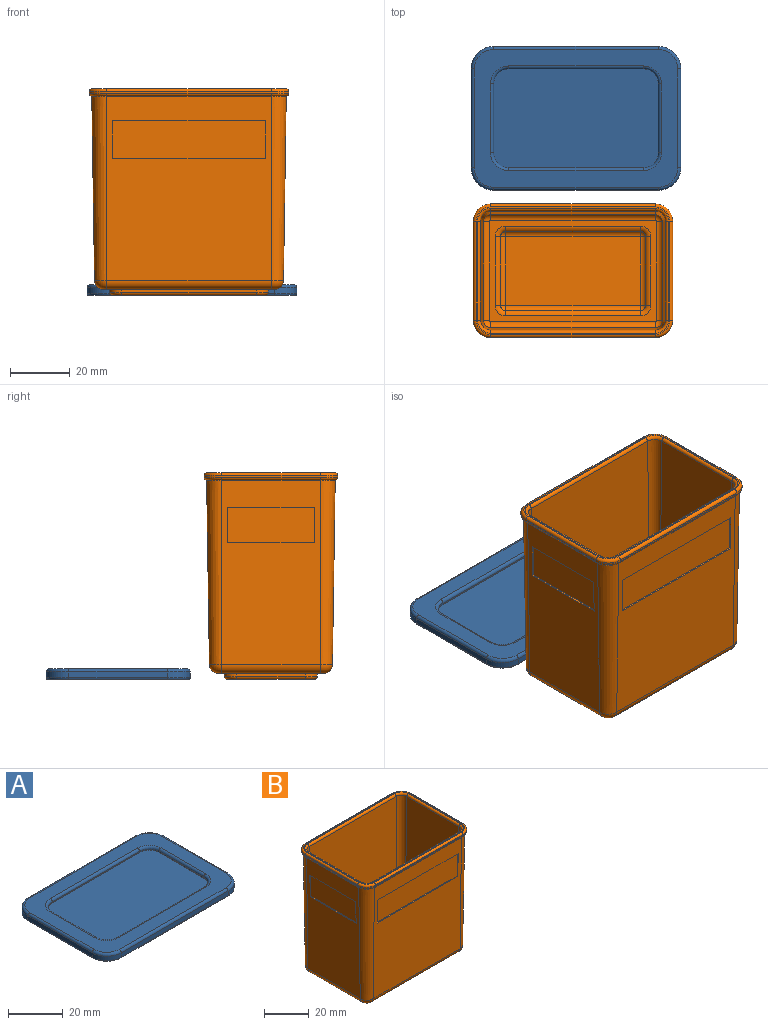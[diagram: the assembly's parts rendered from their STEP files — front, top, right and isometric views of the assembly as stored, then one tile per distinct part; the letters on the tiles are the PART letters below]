
ASSEMBLY  parts=2 mates=1
PART A: 61 faces, bbox 71.2x49.2x3.5 mm
  f0: plane 68x46mm, normal (0,0,-1), area 950.8mm2, adj f5,f6,f7,f9,f10,f11,f19,f20
  f1: plane 55x2mm, normal (0,1,0), area 110mm2, adj f2,f17,f41,f49
  f2: cylinder r=7.5mm len=7.5mm, axis (0,0,-1), area 23.6mm2, adj f1,f3,f39,f47
  f3: plane 33x2mm, normal (-1,0,0), area 66mm2, adj f2,f26,f37,f45
  f4: plane 68x46mm, normal (0,0,1), area 1127.6mm2, adj f37,f38,f39,f40,f41,f42,f43,f44
  f5: plane 55x2.5mm, normal (0,-1,0), area 137.5mm2, adj f0,f6,f8,f19
  f6: cylinder r=6.5mm len=6.5mm, axis (0,0,1), area 25.5mm2, adj f0,f5,f7,f8
  f7: plane 33x2.5mm, normal (1,0,0), area 82.5mm2, adj f0,f6,f8,f28
  f8: plane 69x47mm, normal (0,0,-1), area 109.2mm2, adj f5,f6,f7,f19,f20,f27,f28,f34
  f9: plane 45x2.5mm, normal (0,1,0), area 112.5mm2, adj f0,f11,f12,f22
  f10: plane 23x2.5mm, normal (-1,0,0), area 57.5mm2, adj f0,f11,f12,f30
  f11: cylinder r=7mm len=7mm, axis (0,0,1), area 27.5mm2, adj f0,f9,f10,f12
  f12: plane 59x37mm, normal (0,0,-1), area 2140.9mm2, adj f9,f10,f11,f21,f22,f29,f30,f35
  f13: plane 45x0.5mm, normal (0,-1,0), area 22.5mm2, adj f14,f16,f23,f53
  f14: cylinder r=5mm len=5mm, axis (0,0,1), area 3.9mm2, adj f13,f15,f16,f54
  f15: plane 23x0.5mm, normal (1,0,0), area 11.5mm2, adj f14,f16,f32,f56
  f16: plane 55x33mm, normal (0,0,1), area 1793.5mm2, adj f13,f14,f15,f23,f24,f31,f32,f36
  f17: cylinder r=7.5mm len=7.5mm, axis (0,0,-1), area 23.6mm2, adj f1,f18,f43,f51
  f18: plane 33x2mm, normal (1,0,0), area 66mm2, adj f17,f33,f44,f52
  f19: cylinder r=6.5mm len=6.5mm, axis (0,0,1), area 25.5mm2, adj f0,f5,f8,f20
  f20: plane 33x2.5mm, normal (-1,0,0), area 82.5mm2, adj f0,f8,f19,f34
  f21: plane 23x2.5mm, normal (1,0,0), area 57.5mm2, adj f0,f12,f22,f35
  f22: cylinder r=7mm len=7mm, axis (0,0,1), area 27.5mm2, adj f0,f9,f12,f21
  f23: cylinder r=5mm len=5mm, axis (0,0,1), area 3.9mm2, adj f13,f16,f24,f55
  f24: plane 23x0.5mm, normal (-1,0,0), area 11.5mm2, adj f16,f23,f36,f57
  f25: plane 55x2mm, normal (0,-1,0), area 110mm2, adj f26,f33,f40,f48
  f26: cylinder r=7.5mm len=7.5mm, axis (0,0,-1), area 23.6mm2, adj f3,f25,f38,f46
  f27: plane 55x2.5mm, normal (0,1,0), area 137.5mm2, adj f0,f8,f28,f34
  f28: cylinder r=6.5mm len=6.5mm, axis (0,0,1), area 25.5mm2, adj f0,f7,f8,f27
  f29: plane 45x2.5mm, normal (0,-1,0), area 112.5mm2, adj f0,f12,f30,f35
  f30: cylinder r=7mm len=7mm, axis (0,0,1), area 27.5mm2, adj f0,f10,f12,f29
  f31: plane 45x0.5mm, normal (0,1,0), area 22.5mm2, adj f16,f32,f36,f60
  f32: cylinder r=5mm len=5mm, axis (0,0,1), area 3.9mm2, adj f15,f16,f31,f58
  f33: cylinder r=7.5mm len=7.5mm, axis (0,0,-1), area 23.6mm2, adj f18,f25,f42,f50
  f34: cylinder r=6.5mm len=6.5mm, axis (0,0,1), area 25.5mm2, adj f0,f8,f20,f27
  f35: cylinder r=7mm len=7mm, axis (0,0,1), area 27.5mm2, adj f0,f12,f21,f29
  f36: cylinder r=5mm len=5mm, axis (0,0,1), area 3.9mm2, adj f16,f24,f31,f59
  f37: cylinder r=1mm len=33mm, axis (0,1,0), area 51.8mm2, adj f3,f4,f38,f39
  f38: torus R=6.5mm, axis (0,0,1), area 17.6mm2, adj f4,f26,f37,f40
  f39: torus R=6.5mm, axis (0,0,1), area 17.6mm2, adj f2,f4,f37,f41
  f40: cylinder r=1mm len=55mm, axis (1,0,0), area 86.4mm2, adj f4,f25,f38,f42
  f41: cylinder r=1mm len=55mm, axis (1,0,0), area 86.4mm2, adj f1,f4,f39,f43
  f42: torus R=6.5mm, axis (0,0,1), area 17.6mm2, adj f4,f33,f40,f44
  f43: torus R=6.5mm, axis (0,0,1), area 17.6mm2, adj f4,f17,f41,f44
  f44: cylinder r=1mm len=33mm, axis (0,1,0), area 51.8mm2, adj f4,f18,f42,f43
  f45: cylinder r=0.5mm len=33mm, axis (0,1,0), area 25.9mm2, adj f3,f8,f46,f47
  f46: torus R=7mm, axis (0,0,-1), area 9mm2, adj f8,f26,f45,f48
  f47: torus R=7mm, axis (0,0,-1), area 9mm2, adj f2,f8,f45,f49
  f48: cylinder r=0.5mm len=55mm, axis (1,0,0), area 43.2mm2, adj f8,f25,f46,f50
  f49: cylinder r=0.5mm len=55mm, axis (1,0,0), area 43.2mm2, adj f1,f8,f47,f51
  f50: torus R=7mm, axis (0,0,-1), area 9mm2, adj f8,f33,f48,f52
  f51: torus R=7mm, axis (0,0,-1), area 9mm2, adj f8,f17,f49,f52
  f52: cylinder r=0.5mm len=33mm, axis (0,1,0), area 25.9mm2, adj f8,f18,f50,f51
  f53: cylinder r=1mm len=45mm, axis (1,0,0), area 70.7mm2, adj f4,f13,f54,f55
  f54: torus R=6mm, axis (0,0,1), area 13.2mm2, adj f4,f14,f53,f56
  f55: torus R=6mm, axis (0,0,1), area 13.2mm2, adj f4,f23,f53,f57
  f56: cylinder r=1mm len=23mm, axis (0,1,0), area 36.1mm2, adj f4,f15,f54,f58
  f57: cylinder r=1mm len=23mm, axis (0,1,0), area 36.1mm2, adj f4,f24,f55,f59
  f58: torus R=6mm, axis (0,0,1), area 13.2mm2, adj f4,f32,f56,f60
  f59: torus R=6mm, axis (0,0,1), area 13.2mm2, adj f4,f36,f57,f60
  f60: cylinder r=1mm len=45mm, axis (1,0,0), area 70.7mm2, adj f4,f31,f58,f59
PART B: 121 faces, bbox 67.6x45.6x69 mm
  f0: plane 61.54x33mm, normal (-1,0,-0.01), area 1688mm2, adj f6,f26,f49,f53,f106,f107,f108,f109
  f1: plane 61.54x55mm, normal (0,-1,-0.01), area 2742.7mm2, adj f26,f33,f52,f56,f101,f102,f103,f104
  f2: plane 55.91x33.91mm, normal (0,0,1), area 351.6mm2, adj f37,f38,f39,f40,f41,f42,f43,f44
  f3: plane 57.09x35.09mm, normal (0,0,-1), area 373mm2, adj f13,f14,f15,f24,f25,f31,f32,f36
  f4: plane 64.6x42.6mm, normal (0,0,1), area 85mm2, adj f61,f62,f63,f64,f65,f66,f67,f68
  f5: plane 61.54x55mm, normal (0,1,-0.01), area 2742.7mm2, adj f6,f18,f45,f57,f111,f112,f113,f114
  f6: cone r=4mm half-angle=0.9deg, axis (0,0,1), area 435.4mm2, adj f0,f5,f47,f55
  f7: plane 62.44x55mm, normal (0,-1,0.01), area 3434.8mm2, adj f8,f20,f37,f69
  f8: cone r=2.4mm half-angle=0.9deg, axis (0,0,1), area 286.4mm2, adj f7,f9,f39,f71
  f9: plane 62.44x33mm, normal (1,0,0.01), area 2060.9mm2, adj f8,f28,f41,f73
  f10: plane 33x0.51mm, normal (-1,0,0), area 16.9mm2, adj f11,f29,f53,f61
  f11: cylinder r=5.8mm len=5.8mm, axis (0,0,-1), area 4.7mm2, adj f10,f12,f55,f63
  f12: plane 55x0.51mm, normal (0,1,0), area 28.2mm2, adj f11,f23,f57,f65
  f13: cylinder r=4mm len=4mm, axis (0,0,1), area 6.3mm2, adj f3,f14,f15,f79
  f14: plane 45x1mm, normal (0,1,0), area 45mm2, adj f3,f13,f24,f81
  f15: plane 23x1mm, normal (-1,0,0), area 23mm2, adj f3,f13,f31,f77
  f16: plane 51x29mm, normal (0,0,-1), area 1471.3mm2, adj f77,f78,f79,f80,f81,f82,f83,f84
  f17: plane 45x23mm, normal (0,0,1), area 1035mm2, adj f85,f88,f89,f92
  f18: cone r=4mm half-angle=0.9deg, axis (0,0,1), area 435.4mm2, adj f5,f19,f46,f59
  f19: plane 61.54x33mm, normal (1,0,-0.01), area 1688mm2, adj f18,f33,f48,f60,f116,f117,f118,f119
  f20: cone r=2.4mm half-angle=0.9deg, axis (0,0,1), area 286.4mm2, adj f7,f21,f38,f70
  f21: plane 62.44x33mm, normal (-1,0,0.01), area 2060.9mm2, adj f20,f34,f40,f72
  f22: plane 33x0.51mm, normal (1,0,0), area 16.9mm2, adj f23,f35,f60,f68
  f23: cylinder r=5.8mm len=5.8mm, axis (0,0,-1), area 4.7mm2, adj f12,f22,f59,f67
  f24: cylinder r=4mm len=4mm, axis (0,0,1), area 6.3mm2, adj f3,f14,f25,f83
  f25: plane 23x1mm, normal (1,0,0), area 23mm2, adj f3,f24,f36,f84
  f26: cone r=4mm half-angle=0.9deg, axis (0,0,1), area 435.4mm2, adj f0,f1,f51,f54
  f27: plane 62.44x55mm, normal (0,1,0.01), area 3434.8mm2, adj f28,f34,f44,f76
  f28: cone r=2.4mm half-angle=0.9deg, axis (0,0,1), area 286.4mm2, adj f9,f27,f43,f75
  f29: cylinder r=5.8mm len=5.8mm, axis (0,0,-1), area 4.7mm2, adj f10,f30,f54,f62
  f30: plane 55x0.51mm, normal (0,-1,0), area 28.2mm2, adj f29,f35,f56,f64
  f31: cylinder r=4mm len=4mm, axis (0,0,1), area 6.3mm2, adj f3,f15,f32,f78
  f32: plane 45x1mm, normal (0,-1,0), area 45mm2, adj f3,f31,f36,f80
  f33: cone r=4mm half-angle=0.9deg, axis (0,0,1), area 435.4mm2, adj f1,f19,f50,f58
  f34: cone r=2.4mm half-angle=0.9deg, axis (0,0,1), area 286.4mm2, adj f21,f27,f42,f74
  f35: cylinder r=5.8mm len=5.8mm, axis (0,0,-1), area 4.7mm2, adj f22,f30,f58,f66
  f36: cylinder r=4mm len=4mm, axis (0,0,1), area 6.3mm2, adj f3,f25,f32,f82
  f37: cylinder r=2mm len=55mm, axis (-1,0,0), area 171.1mm2, adj f2,f7,f38,f39
  f38: torus R=0.45mm, axis (0,0,1), area 8.4mm2, adj f2,f20,f37,f40
  f39: torus R=0.45mm, axis (0,0,1), area 8.4mm2, adj f2,f8,f37,f41
  f40: cylinder r=2mm len=33mm, axis (0,1,0), area 102.7mm2, adj f2,f21,f38,f42
  f41: cylinder r=2mm len=33mm, axis (0,1,0), area 102.7mm2, adj f2,f9,f39,f43
  f42: torus R=0.45mm, axis (0,0,1), area 8.4mm2, adj f2,f34,f40,f44
  f43: torus R=0.45mm, axis (0,0,1), area 8.4mm2, adj f2,f28,f41,f44
  f44: cylinder r=2mm len=55mm, axis (-1,0,0), area 171.1mm2, adj f2,f27,f42,f43
  f45: cylinder r=3mm len=55mm, axis (1,0,0), area 256.7mm2, adj f3,f5,f46,f47
  f46: torus R=1.04mm, axis (0,0,1), area 21.6mm2, adj f3,f18,f45,f48
  f47: torus R=1.04mm, axis (0,0,1), area 21.6mm2, adj f3,f6,f45,f49
  f48: cylinder r=3mm len=33mm, axis (0,-1,0), area 154mm2, adj f3,f19,f46,f50
  f49: cylinder r=3mm len=33mm, axis (0,-1,0), area 154mm2, adj f0,f3,f47,f51
  f50: torus R=1.04mm, axis (0,0,1), area 21.6mm2, adj f3,f33,f48,f52
  f51: torus R=1.04mm, axis (0,0,1), area 21.6mm2, adj f3,f26,f49,f52
  f52: cylinder r=3mm len=55mm, axis (1,0,0), area 256.7mm2, adj f1,f3,f50,f51
  f53: cylinder r=1mm len=33mm, axis (0,-1,0), area 46.4mm2, adj f0,f10,f54,f55
  f54: torus R=4.8mm, axis (0,0,-1), area 12.2mm2, adj f26,f29,f53,f56
  f55: torus R=4.8mm, axis (0,0,-1), area 12.2mm2, adj f6,f11,f53,f57
  f56: cylinder r=1mm len=55mm, axis (-1,0,0), area 77.4mm2, adj f1,f30,f54,f58
  f57: cylinder r=1mm len=55mm, axis (1,0,0), area 77.4mm2, adj f5,f12,f55,f59
  f58: torus R=4.8mm, axis (0,0,-1), area 12.2mm2, adj f33,f35,f56,f60
  f59: torus R=4.8mm, axis (0,0,-1), area 12.2mm2, adj f18,f23,f57,f60
  f60: cylinder r=1mm len=33mm, axis (0,1,0), area 46.4mm2, adj f19,f22,f58,f59
  f61: cylinder r=1mm len=33mm, axis (0,1,0), area 51.8mm2, adj f4,f10,f62,f63
  f62: torus R=4.8mm, axis (0,0,1), area 13.4mm2, adj f4,f29,f61,f64
  f63: torus R=4.8mm, axis (0,0,1), area 13.4mm2, adj f4,f11,f61,f65
  f64: cylinder r=1mm len=55mm, axis (1,0,0), area 86.4mm2, adj f4,f30,f62,f66
  f65: cylinder r=1mm len=55mm, axis (1,0,0), area 86.4mm2, adj f4,f12,f63,f67
  f66: torus R=4.8mm, axis (0,0,1), area 13.4mm2, adj f4,f35,f64,f68
  f67: torus R=4.8mm, axis (0,0,1), area 13.4mm2, adj f4,f23,f65,f68
  f68: cylinder r=1mm len=33mm, axis (0,1,0), area 51.8mm2, adj f4,f22,f66,f67
  f69: cylinder r=1mm len=55mm, axis (1,0,0), area 85.6mm2, adj f4,f7,f70,f71
  f70: torus R=4.39mm, axis (0,0,1), area 9.2mm2, adj f4,f20,f69,f72
  f71: torus R=4.39mm, axis (0,0,1), area 9.2mm2, adj f4,f8,f69,f73
  f72: cylinder r=1mm len=33mm, axis (0,-1,0), area 51.3mm2, adj f4,f21,f70,f74
  f73: cylinder r=1mm len=33mm, axis (0,-1,0), area 51.3mm2, adj f4,f9,f71,f75
  f74: torus R=4.39mm, axis (0,0,1), area 9.2mm2, adj f4,f34,f72,f76
  f75: torus R=4.39mm, axis (0,0,1), area 9.2mm2, adj f4,f28,f73,f76
  f76: cylinder r=1mm len=55mm, axis (1,0,0), area 85.6mm2, adj f4,f27,f74,f75
  f77: cylinder r=1mm len=23mm, axis (0,-1,0), area 36.1mm2, adj f15,f16,f78,f79
  f78: torus R=3mm, axis (0,0,-1), area 9mm2, adj f16,f31,f77,f80
  f79: torus R=3mm, axis (0,0,-1), area 9mm2, adj f13,f16,f77,f81
  f80: cylinder r=1mm len=45mm, axis (-1,0,0), area 70.7mm2, adj f16,f32,f78,f82
  f81: cylinder r=1mm len=45mm, axis (-1,0,0), area 70.7mm2, adj f14,f16,f79,f83
  f82: torus R=3mm, axis (0,0,-1), area 9mm2, adj f16,f36,f80,f84
  f83: torus R=3mm, axis (0,0,-1), area 9mm2, adj f16,f24,f81,f84
  f84: cylinder r=1mm len=23mm, axis (0,-1,0), area 36.1mm2, adj f16,f25,f82,f83
  f85: cylinder r=2mm len=45mm, axis (-1,0,0), area 94.2mm2, adj f17,f86,f87,f93
  f86: sphere r=2mm, area 3.1mm2, adj f85,f88,f94
  f87: sphere r=2mm, area 3.1mm2, adj f85,f89,f95
  f88: cylinder r=2mm len=23mm, axis (0,-1,0), area 48.2mm2, adj f17,f86,f90,f96
  f89: cylinder r=2mm len=23mm, axis (0,-1,0), area 48.2mm2, adj f17,f87,f91,f97
  f90: sphere r=2mm, area 3.1mm2, adj f88,f92,f98
  f91: sphere r=2mm, area 3.1mm2, adj f89,f92,f99
  f92: cylinder r=2mm len=45mm, axis (-1,0,0), area 94.2mm2, adj f17,f90,f91,f100
  f93: cylinder r=2mm len=45mm, axis (-1,0,0), area 94.2mm2, adj f2,f85,f94,f95
  f94: torus R=3.46mm, axis (0,0,1), area 8.3mm2, adj f2,f86,f93,f96
  f95: torus R=3.46mm, axis (0,0,1), area 8.3mm2, adj f2,f87,f93,f97
  f96: cylinder r=2mm len=23mm, axis (0,-1,0), area 48.2mm2, adj f2,f88,f94,f98
  f97: cylinder r=2mm len=23mm, axis (0,-1,0), area 48.2mm2, adj f2,f89,f95,f99
  f98: torus R=3.46mm, axis (0,0,1), area 8.3mm2, adj f2,f90,f96,f100
  f99: torus R=3.46mm, axis (0,0,1), area 8.3mm2, adj f2,f91,f97,f100
  f100: cylinder r=2mm len=45mm, axis (-1,0,0), area 94.2mm2, adj f2,f92,f98,f99
  f101: plane 12.61x0.69mm, normal (-1,0,0), area 6.3mm2, adj f1,f102,f104,f105
  f102: plane 51x0.5mm, normal (0,0.01,-1), area 25.5mm2, adj f1,f101,f103,f105
  f103: plane 12.61x0.69mm, normal (1,0,0), area 6.3mm2, adj f1,f102,f104,f105
  f104: plane 51x0.5mm, normal (0,-0.01,1), area 25.5mm2, adj f1,f101,f103,f105
  f105: plane 51x12.6mm, normal (0,-1,-0.01), area 642.6mm2, adj f101,f102,f103,f104
  f106: plane 29x0.5mm, normal (-0.01,0,1), area 14.5mm2, adj f0,f107,f109,f110
  f107: plane 11.84x0.68mm, normal (0,1,0), area 5.9mm2, adj f0,f106,f108,f110
  f108: plane 29x0.5mm, normal (0.01,0,-1), area 14.5mm2, adj f0,f107,f109,f110
  f109: plane 11.84x0.68mm, normal (0,-1,0), area 5.9mm2, adj f0,f106,f108,f110
  f110: plane 29x11.83mm, normal (-1,0,-0.01), area 343.2mm2, adj f106,f107,f108,f109
  f111: plane 12.61x0.69mm, normal (-1,0,0), area 6.3mm2, adj f5,f112,f114,f115
  f112: plane 51x0.5mm, normal (0,0.01,1), area 25.5mm2, adj f5,f111,f113,f115
  f113: plane 12.61x0.69mm, normal (1,0,0), area 6.3mm2, adj f5,f112,f114,f115
  f114: plane 51x0.5mm, normal (0,-0.01,-1), area 25.5mm2, adj f5,f111,f113,f115
  f115: plane 51x12.6mm, normal (0,1,-0.01), area 642.6mm2, adj f111,f112,f113,f114
  f116: plane 29x0.5mm, normal (0.01,0,1), area 14.5mm2, adj f19,f117,f119,f120
  f117: plane 11.84x0.68mm, normal (0,-1,0), area 5.9mm2, adj f19,f116,f118,f120
  f118: plane 29x0.5mm, normal (-0.01,0,-1), area 14.5mm2, adj f19,f117,f119,f120
  f119: plane 11.84x0.68mm, normal (0,1,0), area 5.9mm2, adj f19,f116,f118,f120
  f120: plane 29x11.83mm, normal (1,0,-0.01), area 343.2mm2, adj f116,f117,f118,f119
PLACE A t=(78.5,0,-0.76)mm
PLACE B t=(77.5,-50.99,65.74)mm
MATE planar B.f16 <-> A.f12  axis (0,0,-1) through (77.5,-50.99,63.74)mm
